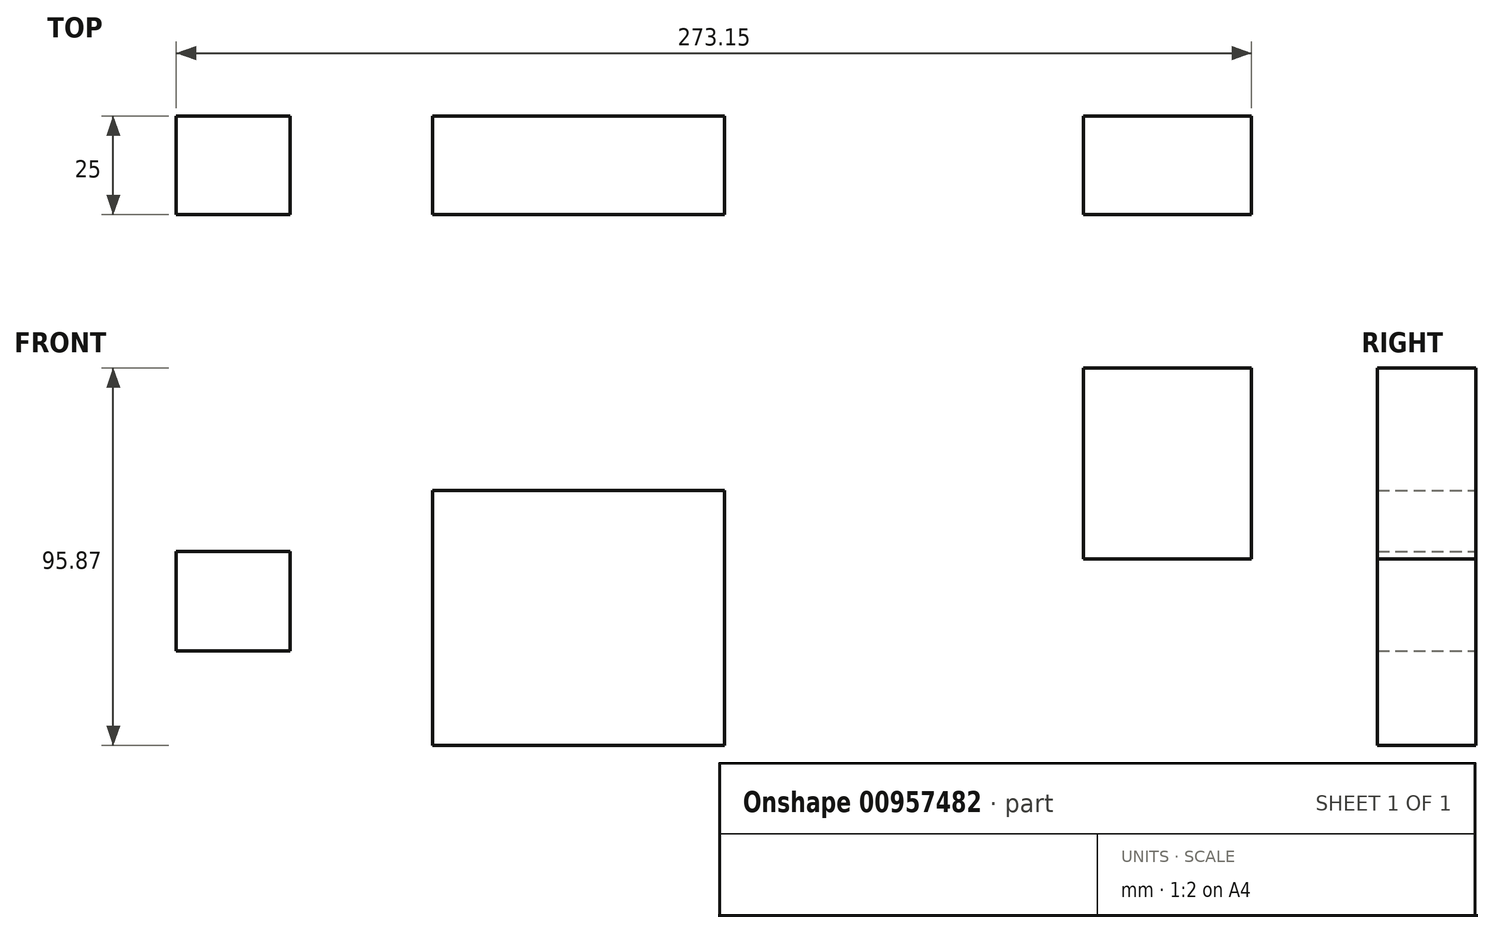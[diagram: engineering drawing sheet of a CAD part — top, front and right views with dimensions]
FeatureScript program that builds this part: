
annotation { "Feature Type Name" : "Feature", "Feature Type Description" : "" }
export const myFeature = defineFeature(function(context is Context, id is Id, definition is map)
    precondition{}
    {
        {
            var Q0;
            Q0=qCreatedBy(makeId("Front.planeOp"),FACE);
            var sketch = newSketch(context, id + "F0", { "sketchPlane" : qUnion([Q0])});
            skLineSegment(sketch, "E0.bottom", {"start": v(-49.44, 52.02) * mm, "end": v(-20.59, 52.02) * mm});
            skLineSegment(sketch, "E0.top", {"start": v(-49.44, 26.74) * mm, "end": v(-20.59, 26.74) * mm});
            skLineSegment(sketch, "E0.left", {"start": v(-49.44, 52.02) * mm, "end": v(-49.44, 26.74) * mm});
            skLineSegment(sketch, "E0.right", {"start": v(-20.59, 52.02) * mm, "end": v(-20.59, 26.74) * mm});
            skSolve(sketch);
        }
        {
            var Q0;
            Q0=makeQuery(id+"F0.imprint","IMPRINT",FACE,{"disambiguationData":[TD([[makeQuery(id+"F0.imprint","IMPRINT",EDGE,{"derivedFrom":sQuery(id+"F0.wireOp",EDGE,"E0.bottom")}),-1.0]])]});
            extrude(context, id + "F1", {"entities" : qUnion([Q0]), "depth" : 25 * mm, "offsetDistance" : 25 * mm});
        }
        {
            var Q0;
            Q0=qCreatedBy(makeId("Front.planeOp"),FACE);
            var sketch = newSketch(context, id + "F2", { "sketchPlane" : qUnion([Q0])});
            skLineSegment(sketch, "E1.bottom", {"start": v(15.63, 67.5) * mm, "end": v(89.86, 67.5) * mm});
            skLineSegment(sketch, "E1.top", {"start": v(15.63, 2.7) * mm, "end": v(89.86, 2.7) * mm});
            skLineSegment(sketch, "E1.left", {"start": v(15.63, 67.5) * mm, "end": v(15.63, 2.7) * mm});
            skLineSegment(sketch, "E1.right", {"start": v(89.86, 67.5) * mm, "end": v(89.86, 2.7) * mm});
            skLineSegment(sketch, "E2.bottom", {"start": v(181.04, 98.58) * mm, "end": v(223.7, 98.58) * mm});
            skLineSegment(sketch, "E2.top", {"start": v(181.04, 50.11) * mm, "end": v(223.7, 50.11) * mm});
            skLineSegment(sketch, "E2.left", {"start": v(181.04, 98.58) * mm, "end": v(181.04, 50.11) * mm});
            skLineSegment(sketch, "E2.right", {"start": v(223.7, 98.58) * mm, "end": v(223.7, 50.11) * mm});
            skSolve(sketch);
        }
        {
            var Q0;
            Q0 = qSketchRegion(id + "F2", true);
            extrude(context, id + "F3", {"entities" : qUnion([Q0]), "depth" : 25 * mm, "offsetDistance" : 25 * mm});
        }
    });
